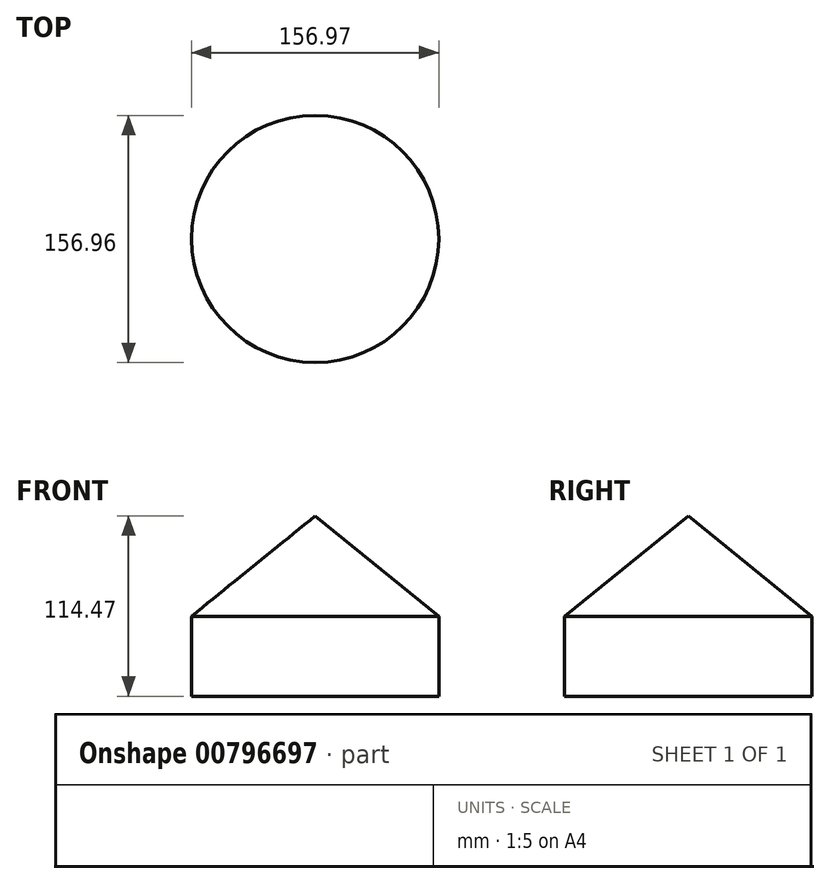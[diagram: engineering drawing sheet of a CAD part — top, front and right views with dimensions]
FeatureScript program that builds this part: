
annotation { "Feature Type Name" : "Feature", "Feature Type Description" : "" }
export const myFeature = defineFeature(function(context is Context, id is Id, definition is map)
    precondition{}
    {
        {
            var Q0;
            Q0=qCreatedBy(makeId("Front.planeOp"),FACE);
            var sketch = newSketch(context, id + "F0", { "sketchPlane" : qUnion([Q0])});
            skPoint(sketch, "E0", {"position": v(78.48, 21.42) * mm});
            skPoint(sketch, "E1", {"position": v(45.46, 0) * mm});
            skPoint(sketch, "E2", {"position": v(78.48, 0) * mm});
            skPoint(sketch, "E3", {"position": v(0, -42.25) * mm});
            skPoint(sketch, "E4", {"position": v(45.46, -42.25) * mm});
            skLineSegment(sketch, "E5", {"start": v(78.48, 21.42) * mm, "end": v(78.48, 0) * mm});
            skLineSegment(sketch, "E6", {"start": v(78.48, -42.25) * mm, "end": v(78.48, 0) * mm});
            skLineSegment(sketch, "E7", {"start": v(78.48, -42.25) * mm, "end": v(45.46, -42.25) * mm});
            skLineSegment(sketch, "E8", {"start": v(0, -42.25) * mm, "end": v(78.48, 21.42) * mm});
            skLineSegment(sketch, "E9", {"start": v(45.46, -42.25) * mm, "end": v(0, -42.25) * mm});
            skSolve(sketch);
        }
        {
            var Q0;
            Q0 = qSketchRegion(id + "F0", true);
            var Q1;
            Q1=sQuery(id+"F0.wireOp",EDGE,"E6");
            revolve(context, id + "F1", {"surfaceOperationType" : NewSurfaceOperationType.NEW, "entities" : qUnion([Q0]), "axis" : qUnion([Q1]), "revolveType" : RevolveType.FULL});
        }
        {
            var Q0;
            Q0=makeQuery(id+"F1.opRevolve","SWEPT_FACE",FACE,{"disambiguationData":[OSD([sQuery(id+"F0.wireOp",EDGE,"E7"),sQuery(id+"F0.wireOp",EDGE,"E9")])]});
            extrude(context, id + "F2", {"entities" : qUnion([Q0]), "operationType" : NewBodyOperationType.ADD, "depth" : 50.8 * mm, "offsetDistance" : 25.4 * mm});
        }
    });
